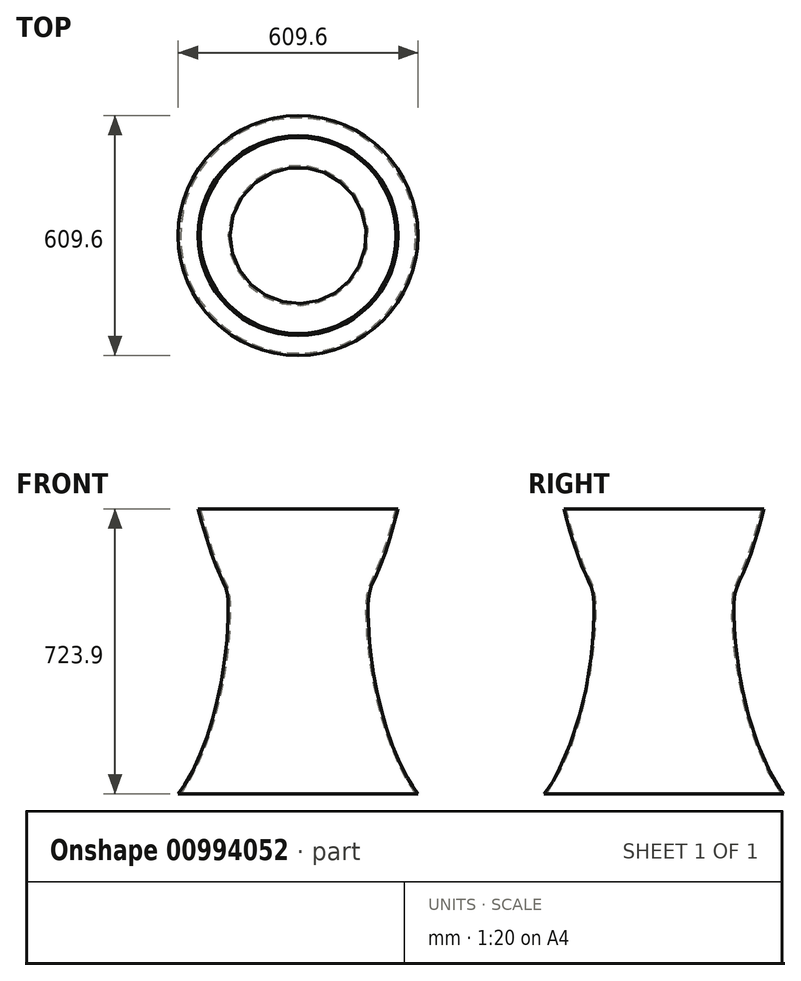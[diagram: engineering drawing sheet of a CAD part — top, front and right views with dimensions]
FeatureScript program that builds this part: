
annotation { "Feature Type Name" : "Feature", "Feature Type Description" : "" }
export const myFeature = defineFeature(function(context is Context, id is Id, definition is map)
    precondition{}
    {
        {
            var Q0;
            Q0=qCreatedBy(makeId("Front.planeOp"),FACE);
            var sketch = newSketch(context, id + "F0", { "sketchPlane" : qUnion([Q0])});
            skFitSpline(sketch, "E0", {"points": [v(-550.03, 231.97) * mm, v(-474.47, 0) * mm, v(-601.56, -495.97) * mm], "startDerivative": vector(395.63, -1480.72) * mm, "endDerivative": vector(-563.48, -789.81) * mm});
            skLineSegment(sketch, "E1", {"start": v(-300.7, 228.6) * mm, "end": v(-300.7, 554.87) * mm, "construction": true});
            skFitSpline(sketch, "E2.0", {"points": [v(-554.7, 230.73) * mm, v(-546.43, 199.83) * mm, v(-531.62, 148.7) * mm, v(-516.91, 105.85) * mm, v(-507.2, 80.89) * mm, v(-500.86, 66) * mm, v(-495.46, 54.13) * mm, v(-490.93, 44.5) * mm, v(-487.26, 36.34) * mm, v(-484.38, 28.85) * mm, v(-482.16, 21.1) * mm, v(-480.75, 13.63) * mm, v(-479.87, 6.58) * mm, v(-479.33, 0.64) * mm, v(-478.9, -6.04) * mm, v(-478.5, -15.93) * mm, v(-478.3, -30) * mm, v(-478.63, -49.38) * mm, v(-479.6, -70.98) * mm, v(-481.23, -94.56) * mm, v(-483.6, -119.87) * mm, v(-487.82, -155.58) * mm, v(-495.18, -203.3) * mm, v(-507.81, -263.51) * mm, v(-524.65, -324.7) * mm, v(-546.12, -384.88) * mm, v(-572.61, -442.08) * mm, v(-593.89, -476.9) * mm, v(-605.5, -493.17) * mm]});
            skLineSegment(sketch, "E3", {"start": v(-554.7, 230.73) * mm, "end": v(-549.7, 230.73) * mm});
            skLineSegment(sketch, "E4", {"start": v(-605.5, -493.17) * mm, "end": v(-599.58, -493.17) * mm});
            skSolve(sketch);
        }
        {
            var Q0;
            Q0=makeQuery(id+"F0.imprint","IMPRINT",FACE,{"disambiguationData":[TD([[makeQuery(id+"F0.imprint","IMPRINT",EDGE,{"derivedFrom":sQuery(id+"F0.wireOp",EDGE,"E0")}),-1.0]])]});
            var Q1;
            Q1=sQuery(id+"F0.wireOp",EDGE,"E1");
            revolve(context, id + "F1", {"surfaceOperationType" : NewSurfaceOperationType.NEW, "entities" : qUnion([Q0]), "axis" : qUnion([Q1]), "revolveType" : RevolveType.FULL});
        }
    });
